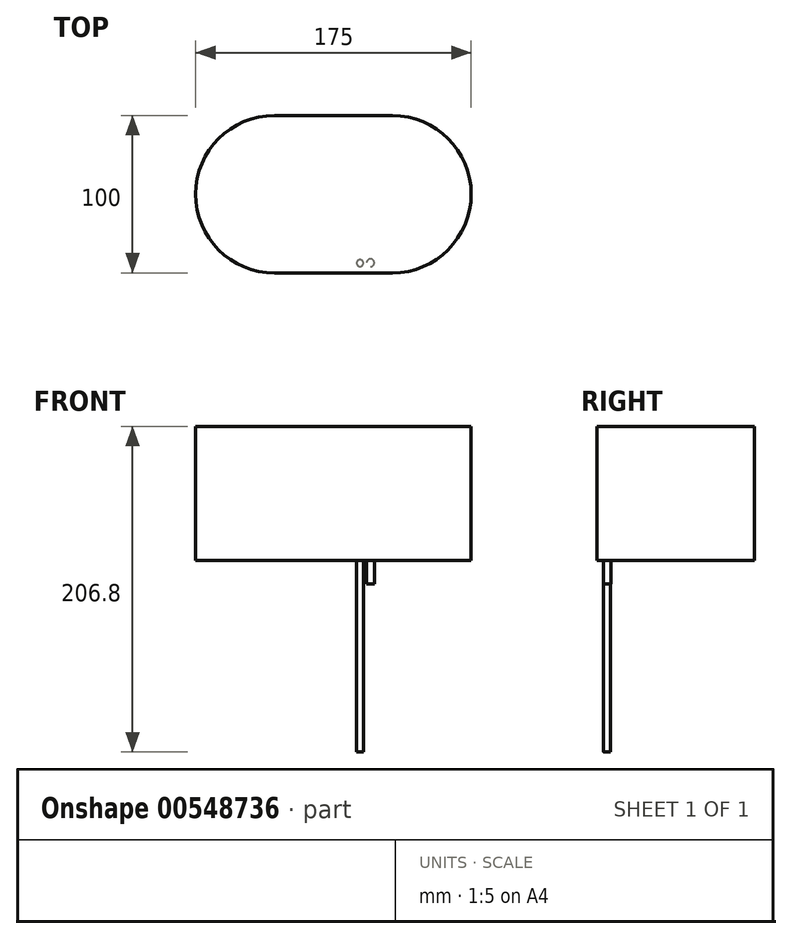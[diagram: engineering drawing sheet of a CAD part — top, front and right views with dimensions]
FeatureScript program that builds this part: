
annotation { "Feature Type Name" : "Feature", "Feature Type Description" : "" }
export const myFeature = defineFeature(function(context is Context, id is Id, definition is map)
    precondition{}
    {
        {
            var Q0;
            Q0=qCreatedBy(makeId("Top.planeOp"),FACE);
            var sketch = newSketch(context, id + "F0", { "sketchPlane" : qUnion([Q0])});
            skLineSegment(sketch, "E0.bottom", {"start": v(0, 0) * mm, "end": v(175, 0) * mm});
            skLineSegment(sketch, "E0.top", {"start": v(0, 100) * mm, "end": v(175, 100) * mm});
            skLineSegment(sketch, "E0.left", {"start": v(0, 0) * mm, "end": v(0, 100) * mm});
            skLineSegment(sketch, "E0.right", {"start": v(175, 0) * mm, "end": v(175, 100) * mm});
            skSolve(sketch);
        }
        {
            var Q0;
            Q0=makeQuery(id+"F0.imprint","IMPRINT",FACE,{"disambiguationData":[TD([[makeQuery(id+"F0.imprint","IMPRINT",EDGE,{"derivedFrom":sQuery(id+"F0.wireOp",EDGE,"E0.bottom")}),1.0]])]});
            extrude(context, id + "F1", {"entities" : qUnion([Q0]), "depth" : 85 * mm, "offsetDistance" : 25 * mm});
        }
        {
            var Q0;
            Q0=makeQuery(id+"F1.opExtrude","SWEPT_EDGE",EDGE,{"disambiguationData":[OSD([sQuery(id+"F0.wireOp",EDGE,"E0.bottom"),sQuery(id+"F0.wireOp",EDGE,"E0.left")])]});
            var Q1;
            Q1=makeQuery(id+"F1.opExtrude","SWEPT_EDGE",EDGE,{"disambiguationData":[OSD([sQuery(id+"F0.wireOp",EDGE,"E0.top"),sQuery(id+"F0.wireOp",EDGE,"E0.left")])]});
            fillet(context, id + "F2", {"entities" : qUnion([Q0, Q1]), "radius" : 50 * mm, "tangentPropagation" : true, "allowEdgeOverflow" : false});
        }
        {
            var Q0;
            Q0=makeQuery(id+"F1.opExtrude","SWEPT_EDGE",EDGE,{"disambiguationData":[OSD([sQuery(id+"F0.wireOp",EDGE,"E0.top"),sQuery(id+"F0.wireOp",EDGE,"E0.right")])]});
            var Q1;
            Q1=makeQuery(id+"F1.opExtrude","SWEPT_EDGE",EDGE,{"disambiguationData":[OSD([sQuery(id+"F0.wireOp",EDGE,"E0.bottom"),sQuery(id+"F0.wireOp",EDGE,"E0.right")])]});
            fillet(context, id + "F3", {"entities" : qUnion([Q0, Q1]), "radius" : 50 * mm, "tangentPropagation" : true, "allowEdgeOverflow" : false});
        }
        {
            var Q0;
            Q0=makeQuery(id+"F1.opExtrude","CAP_FACE",FACE,{"disambiguationData":[OSD([sQuery(id+"F0.wireOp",EDGE,"E0.bottom"),sQuery(id+"F0.wireOp",EDGE,"E0.top"),sQuery(id+"F0.wireOp",EDGE,"E0.left"),sQuery(id+"F0.wireOp",EDGE,"E0.right")])],"isStart":true});
            var sketch = newSketch(context, id + "F4", { "sketchPlane" : qUnion([Q0])});
            skCircle(sketch, "E1", {"center": v(121.53, -6.7) * mm, "radius": 4.3 * mm});
            skCircle(sketch, "E2", {"center": v(112.34, -6.57) * mm, "radius": 1.74 * mm});
            skLineSegment(sketch, "E3.bottom", {"start": v(98.53, -8.54) * mm, "end": v(107.77, -8.54) * mm});
            skLineSegment(sketch, "E3.top", {"start": v(98.53, -4.81) * mm, "end": v(107.77, -4.81) * mm});
            skLineSegment(sketch, "E3.left", {"start": v(98.53, -8.54) * mm, "end": v(98.53, -4.81) * mm});
            skLineSegment(sketch, "E3.right", {"start": v(107.77, -8.54) * mm, "end": v(107.77, -4.81) * mm});
            skPoint(sketch, "E3.middle", {"position": v(103.15, -6.68) * mm});
            skSolve(sketch);
        }
        {
            var Q0;
            Q0=sQuery(id+"F4.wireOp",EDGE,"E1");
            extrude(context, id + "F5", {"bodyType" : ToolBodyType.SURFACE, "surfaceEntities" : qUnion([Q0]), "depth" : 8 * mm, "offsetDistance" : 25 * mm});
        }
        {
            var Q0;
            Q0=makeQuery(id+"F1.opExtrude","CAP_FACE",FACE,{"disambiguationData":[OSD([sQuery(id+"F0.wireOp",EDGE,"E0.bottom"),sQuery(id+"F0.wireOp",EDGE,"E0.top"),sQuery(id+"F0.wireOp",EDGE,"E0.left"),sQuery(id+"F0.wireOp",EDGE,"E0.right")])],"isStart":true});
            var sketch = newSketch(context, id + "F6", { "sketchPlane" : qUnion([Q0])});
            skCircle(sketch, "E4", {"center": v(111.06, -6.45) * mm, "radius": 2.42 * mm});
            skSolve(sketch);
        }
        {
            var Q0;
            Q0=makeQuery(id+"F6.imprint","IMPRINT",FACE,{"disambiguationData":[TD([[makeQuery(id+"F6.imprint","IMPRINT",EDGE,{"derivedFrom":sQuery(id+"F6.wireOp",EDGE,"E4")}),1.0]])]});
            extrude(context, id + "F7", {"entities" : qUnion([Q0]), "operationType" : NewBodyOperationType.ADD, "depth" : 15.2 * mm, "offsetDistance" : 25 * mm});
        }
        {
            var Q0;
            Q0=makeQuery(id+"F1.opExtrude","CAP_FACE",FACE,{"disambiguationData":[OSD([sQuery(id+"F0.wireOp",EDGE,"E0.bottom"),sQuery(id+"F0.wireOp",EDGE,"E0.top"),sQuery(id+"F0.wireOp",EDGE,"E0.left"),sQuery(id+"F0.wireOp",EDGE,"E0.right")])],"isStart":true});
            var sketch = newSketch(context, id + "F8", { "sketchPlane" : qUnion([Q0])});
            skCircle(sketch, "E5", {"center": v(104.43, -6.22) * mm, "radius": 2.14 * mm});
            skSolve(sketch);
        }
        {
            var Q0;
            Q0=makeQuery(id+"F8.imprint","IMPRINT",FACE,{"disambiguationData":[TD([[makeQuery(id+"F8.imprint","IMPRINT",EDGE,{"derivedFrom":sQuery(id+"F8.wireOp",EDGE,"E5")}),1.0]])]});
            extrude(context, id + "F9", {"entities" : qUnion([Q0]), "operationType" : NewBodyOperationType.ADD, "depth" : 121.8 * mm, "offsetDistance" : 25 * mm});
        }
    });
